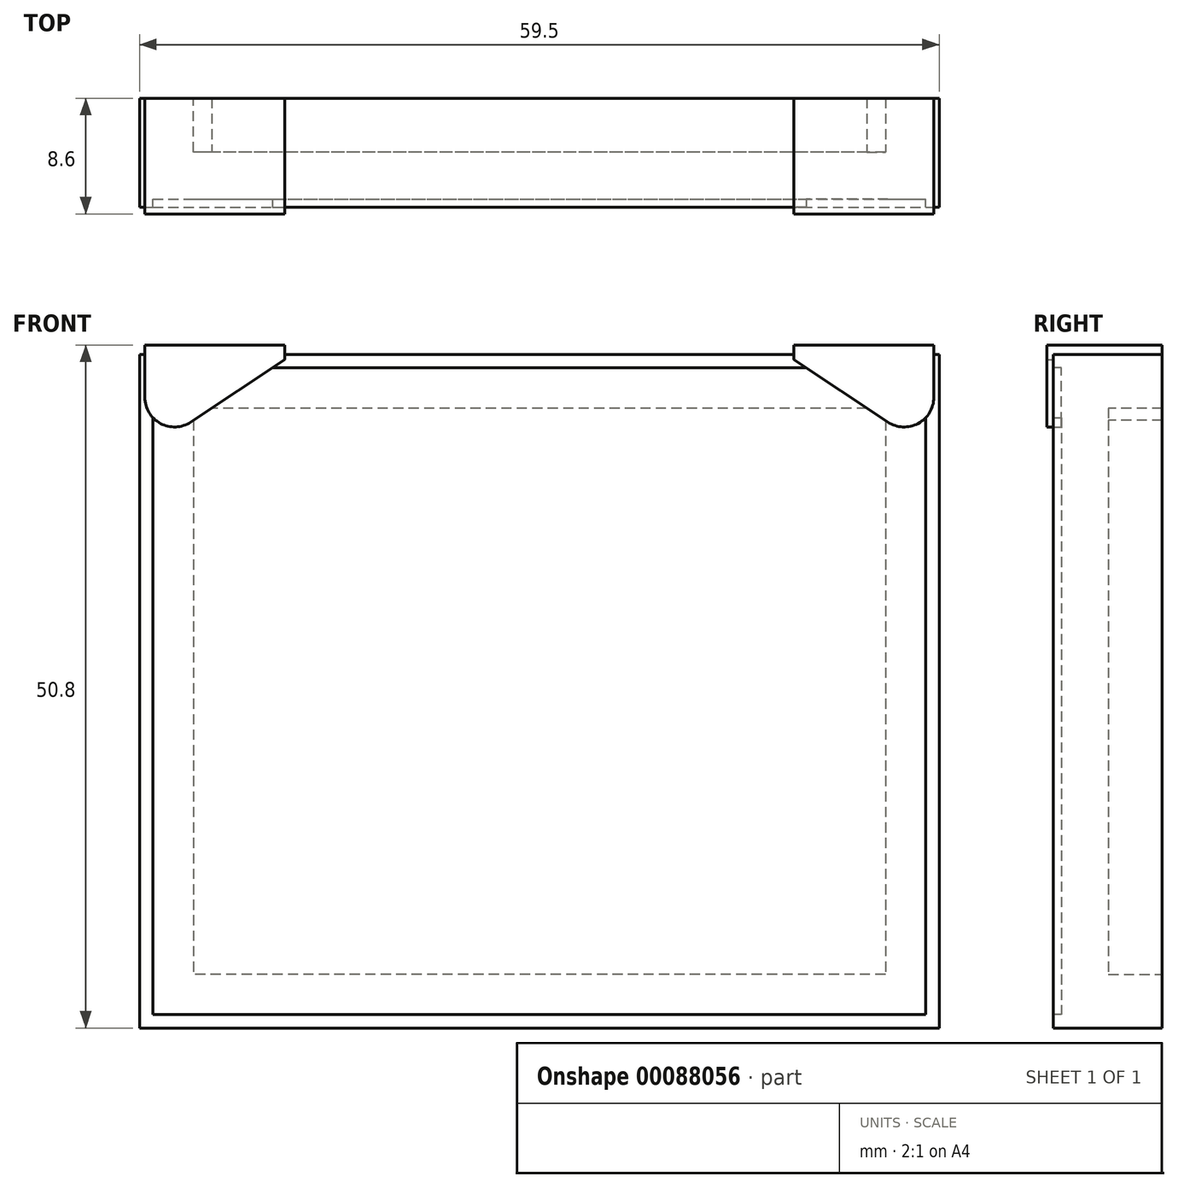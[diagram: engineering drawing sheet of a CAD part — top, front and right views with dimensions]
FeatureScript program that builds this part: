
annotation { "Feature Type Name" : "Feature", "Feature Type Description" : "" }
export const myFeature = defineFeature(function(context is Context, id is Id, definition is map)
    precondition{}
    {
        {
            var Q0;
            Q0=qCreatedBy(makeId("Front.planeOp"),FACE);
            var sketch = newSketch(context, id + "F0", { "sketchPlane" : qUnion([Q0])});
            skLineSegment(sketch, "E0.bottom", {"start": v(-29.75, 25.05) * mm, "end": v(29.75, 25.05) * mm});
            skLineSegment(sketch, "E0.top", {"start": v(-29.75, -25.05) * mm, "end": v(29.75, -25.05) * mm});
            skLineSegment(sketch, "E0.left", {"start": v(-29.75, 25.05) * mm, "end": v(-29.75, -25.05) * mm});
            skLineSegment(sketch, "E0.right", {"start": v(29.75, 25.05) * mm, "end": v(29.75, -25.05) * mm});
            skPoint(sketch, "E0.middle", {"position": v(0, 0) * mm});
            skSolve(sketch);
        }
        {
            var Q0;
            Q0 = qSketchRegion(id + "F0", true);
            extrude(context, id + "F1", {"entities" : qUnion([Q0]), "depth" : 8.1 * mm, "offsetDistance" : 25 * mm});
        }
        {
            var Q0;
            Q0=makeQuery(id+"F1.opExtrude","CAP_FACE",FACE,{"disambiguationData":[OSD([sQuery(id+"F0.wireOp",EDGE,"E0.bottom"),sQuery(id+"F0.wireOp",EDGE,"E0.top"),sQuery(id+"F0.wireOp",EDGE,"E0.left"),sQuery(id+"F0.wireOp",EDGE,"E0.right")])],"isStart":false});
            var sketch = newSketch(context, id + "F2", { "sketchPlane" : qUnion([Q0])});
            skLineSegment(sketch, "E1.bottom", {"start": v(-28.75, 24.05) * mm, "end": v(28.75, 24.05) * mm});
            skLineSegment(sketch, "E1.top", {"start": v(-28.75, -24.05) * mm, "end": v(28.75, -24.05) * mm});
            skLineSegment(sketch, "E1.left", {"start": v(-28.75, 24.05) * mm, "end": v(-28.75, -24.05) * mm});
            skLineSegment(sketch, "E1.right", {"start": v(28.75, 24.05) * mm, "end": v(28.75, -24.05) * mm});
            skPoint(sketch, "E1.middle", {"position": v(0, 0) * mm});
            skSolve(sketch);
        }
        {
            var Q0;
            Q0 = qSketchRegion(id + "F2", true);
            extrude(context, id + "F3", {"entities" : qUnion([Q0]), "operationType" : NewBodyOperationType.REMOVE, "oppositeDirection" : true, "depth" : .6 * mm, "offsetDistance" : 25 * mm});
        }
        {
            var Q0;
            Q0=makeQuery(id+"F1.opExtrude","CAP_FACE",FACE,{"disambiguationData":[OSD([sQuery(id+"F0.wireOp",EDGE,"E0.bottom"),sQuery(id+"F0.wireOp",EDGE,"E0.top"),sQuery(id+"F0.wireOp",EDGE,"E0.left"),sQuery(id+"F0.wireOp",EDGE,"E0.right")])],"isStart":true});
            var sketch = newSketch(context, id + "F4", { "sketchPlane" : qUnion([Q0])});
            skLineSegment(sketch, "E2.bottom", {"start": v(-25.75, 21.05) * mm, "end": v(25.75, 21.05) * mm});
            skLineSegment(sketch, "E2.top", {"start": v(-25.75, -21.05) * mm, "end": v(25.75, -21.05) * mm});
            skLineSegment(sketch, "E2.left", {"start": v(-25.75, 21.05) * mm, "end": v(-25.75, -21.05) * mm});
            skLineSegment(sketch, "E2.right", {"start": v(25.75, 21.05) * mm, "end": v(25.75, -21.05) * mm});
            skPoint(sketch, "E2.middle", {"position": v(0, 0) * mm});
            skSolve(sketch);
        }
        {
            var Q0;
            Q0 = qSketchRegion(id + "F4", true);
            extrude(context, id + "F5", {"entities" : qUnion([Q0]), "operationType" : NewBodyOperationType.REMOVE, "oppositeDirection" : true, "depth" : 4 * mm, "offsetDistance" : 25 * mm});
        }
        {
            var Q0;
            Q0=makeQuery(id+"F1.opExtrude","CAP_FACE",FACE,{"disambiguationData":[OSD([sQuery(id+"F0.wireOp",EDGE,"E0.bottom"),sQuery(id+"F0.wireOp",EDGE,"E0.top"),sQuery(id+"F0.wireOp",EDGE,"E0.left"),sQuery(id+"F0.wireOp",EDGE,"E0.right")])],"isStart":false});
            var sketch = newSketch(context, id + "F6", { "sketchPlane" : qUnion([Q0])});
            skLineSegment(sketch, "E3", {"start": v(0, 0) * mm, "end": v(0, 20.8) * mm, "construction": true});
            skLineSegment(sketch, "E4", {"start": v(29.35, 21.85) * mm, "end": v(29.35, 25.75) * mm});
            skLineSegment(sketch, "E5", {"start": v(29.35, 25.75) * mm, "end": v(18.95, 25.75) * mm});
            skLineSegment(sketch, "E6", {"start": v(18.95, 25.75) * mm, "end": v(18.95, 24.65) * mm});
            skArc(sketch, "E7", {"start": v(25.93, 20.02) * mm, "mid": v(28.2, 19.91) * mm, "end": v(29.35, 21.85) * mm});
            skLineSegment(sketch, "E8", {"start": v(18.95, 24.65) * mm, "end": v(25.93, 20.02) * mm});
            skLineSegment(sketch, "E9.MirrorCS", {"start": v(-18.95, 25.75) * mm, "end": v(-18.95, 24.65) * mm});
            skArc(sketch, "E10.MirrorCS", {"start": v(-25.93, 20.02) * mm, "mid": v(-28.2, 19.91) * mm, "end": v(-29.35, 21.85) * mm});
            skLineSegment(sketch, "E11.MirrorCS", {"start": v(-29.35, 25.75) * mm, "end": v(-18.95, 25.75) * mm});
            skLineSegment(sketch, "E12.MirrorCS", {"start": v(-18.95, 24.65) * mm, "end": v(-25.93, 20.02) * mm});
            skLineSegment(sketch, "E13.MirrorCS", {"start": v(-29.35, 21.85) * mm, "end": v(-29.35, 25.75) * mm});
            skSolve(sketch);
        }
        {
            var Q0;
            Q0 = qSketchRegion(id + "F6", true);
            extrude(context, id + "F7", {"entities" : qUnion([Q0]), "operationType" : NewBodyOperationType.ADD, "depth" : .5 * mm, "offsetDistance" : 25 * mm, "hasSecondDirection" : true, "secondDirectionOppositeDirection" : true, "secondDirectionDepth" : 8.1 * mm});
        }
    });
